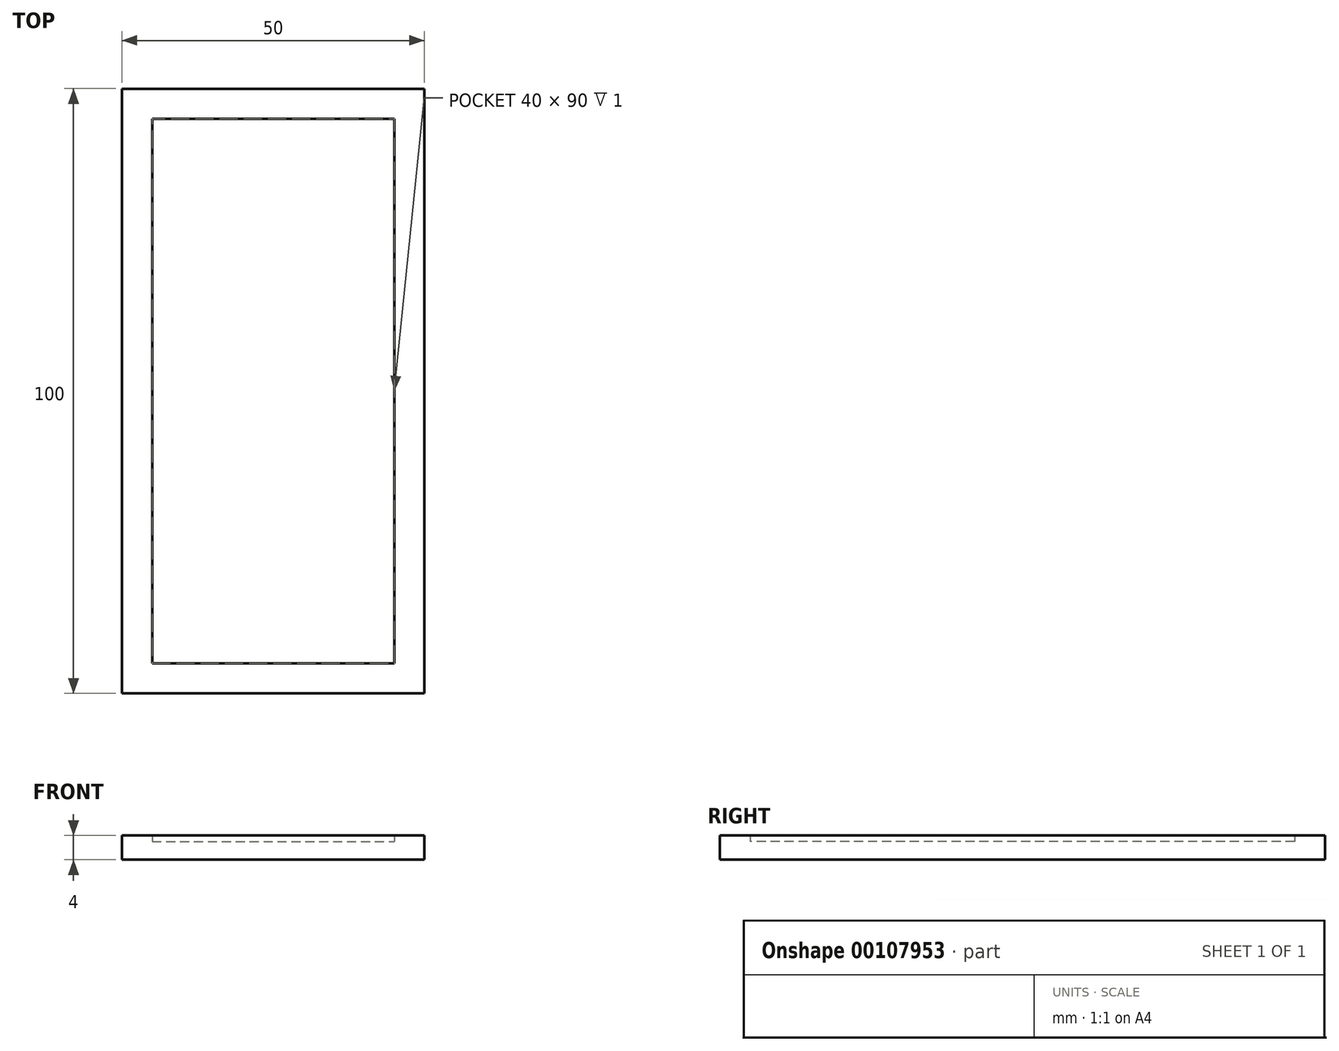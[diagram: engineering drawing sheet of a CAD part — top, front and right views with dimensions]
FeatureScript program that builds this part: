
annotation { "Feature Type Name" : "Feature", "Feature Type Description" : "" }
export const myFeature = defineFeature(function(context is Context, id is Id, definition is map)
    precondition{}
    {
        {
            var Q0;
            Q0=qCreatedBy(makeId("Top.planeOp"),FACE);
            var sketch = newSketch(context, id + "F0", { "sketchPlane" : qUnion([Q0])});
            skLineSegment(sketch, "E0.bottom", {"start": v(-45, 41.27) * mm, "end": v(5, 41.27) * mm});
            skLineSegment(sketch, "E0.top", {"start": v(-45, -58.73) * mm, "end": v(5, -58.73) * mm});
            skLineSegment(sketch, "E0.left", {"start": v(-45, 41.27) * mm, "end": v(-45, -58.73) * mm});
            skLineSegment(sketch, "E0.right", {"start": v(5, 41.27) * mm, "end": v(5, -58.73) * mm});
            skLineSegment(sketch, "E1.bottom", {"start": v(-40, 36.27) * mm, "end": v(0, 36.27) * mm});
            skLineSegment(sketch, "E1.top", {"start": v(-40, -53.73) * mm, "end": v(0, -53.73) * mm});
            skLineSegment(sketch, "E1.left", {"start": v(-40, 36.27) * mm, "end": v(-40, -53.73) * mm});
            skLineSegment(sketch, "E1.right", {"start": v(0, 36.27) * mm, "end": v(0, -53.73) * mm});
            skSolve(sketch);
        }
        {
            var Q0;
            Q0 = qSketchRegion(id + "F0", true);
            extrude(context, id + "F1", {"entities" : qUnion([Q0]), "depth" : 4 * mm});
        }
        {
            var Q0;
            Q0=makeQuery(id+"F0.imprint","IMPRINT",FACE,{"disambiguationData":[TD([[makeQuery(id+"F0.imprint","IMPRINT",EDGE,{"derivedFrom":sQuery(id+"F0.wireOp",EDGE,"E1.bottom")}),-1.0]])]});
            extrude(context, id + "F2", {"entities" : qUnion([Q0]), "operationType" : NewBodyOperationType.ADD, "depth" : 3 * mm});
        }
    });
